# Revit family: RN 11030 Réducteur de pression avec filetage femelle
name_source: partatom
category: Rohrzubehör
units: mm (PartAtom-declared; Revit-internal decimal feet)

## family parameters
Arbeitsebenenbasiert = Nein
Beim Laden mit Abzugskörper schneiden = Nein
Bemaßung runder Anschluss = Durchmesser verwenden
Gemeinsam genutzt = Nein
Immer vertikal = Ja
Teiletyp = Ventil - Zerlegung in

## types (3) — shared parameters
1.010.00.2 Blattnummer der Richtlinie = 17
1.010.00.3 Ausgabedatum (Monat) der Richtlinie = 201601
1.010.00.4 Herstellername = R. Nussbaum AG
1.010.00.5 Revisionsdatum der Datei = 20190528
1.010.00.6 Webadresse des Herstellers = http://www.nussbaum.ch
1.100.00.3 Sortiernummer für Anzeigereihenfolge = 8
1.100.00.4 Produktbezeichnung = Druckminderer
1.960/3L.00.8 Link (URL) = https://www.nussbaum.ch
17.700.00.4 Armaturentyp = 8
17.700.00.7 Maximale Betriebstemperatur TB [°C] = 30
17.700.00.8 Maximaler Betriebsdruck (Arbeitsdruck) ps [1.0 · 105 Pa] = 16
Connector Visibility = Nein
EnclosingSpace Visibility = Nein
Hersteller = R. Nussbauzm AG
URL = https://www.nussbaum.ch

## per-type parameters (varying)
| type | 1.800.00.3 TGA-Nummer | 1.810.00.3 Hersteller-Bestellnummer | 1.810.00.4 DATANORM-Nummer | 1.810.00.5 StLB-Nummer | 1.810.00.6 GTIN-Nummer | 17.700.00.30 Produktbeschreibung | 17.700.00.5 Nennweite DN | 17.700.00.6 kvs-Wert [m3/h] | CONNECTOR0_DIAMETER_dX_0r | CONNECTOR0_dX_00 | CONNECTOR0_dX_01 | CONNECTOR0_ref_dX | CONNECTOR1_DIAMETER_dX_0r | CONNECTOR1_dX_00 | CONNECTOR1_dX_01 | CONNECTOR1_ref_dX | Modell | R. Nussbaum AG 11030.03 de Visibility | R. Nussbaum AG 11030.04 de Visibility | R. Nussbaum AG 11030.05 de Visibility | Typenkommentare |
| DN 10 | 0080050000000000000000000000020070000000000000000100000000 | 11030.03 | 11030.03 | 613.112 | 7612945694799 | 11030.03, Druckreduzierventil mit Innengewinde, Einstellbereich 1 bis 5 bar, DN=1 | 10 | 0.78 | 10 mm  [stored 0.0328084 ft] | 38 mm | 23 mm | 23 mm | 10 mm  [stored 0.0328084 ft] | 23 mm | 38 mm | 23 mm | 11030.03 | Ja | Nein | Nein | Réducteur de pression avec filetage femelleDN 10 |
| DN 15 | 0080050000000000000000000000020070000000000000000200000000 | 11030.04 | 11030.04 | 613.113 | 7612945694805 | 11030.04, Druckreduzierventil mit Innengewinde, Einstellbereich 1 bis 5 bar, DN=1 | 15 | 1.2 | 15 mm | 43 mm | 28 mm | 28 mm | 15 mm | 28 mm | 43 mm | 28 mm | 11030.04 | Nein | Ja | Nein | Réducteur de pression avec filetage femelleDN 15 |
| DN 20 | 0080050000000000000000000000020070000000000000000300000000 | 11030.05 | 11030.05 | 613.114 | 7612945694812 | 11030.05, Druckreduzierventil mit Innengewinde, Einstellbereich 1 bis 5 bar, DN=2 | 20 | 1.62 | 20 mm | 48 mm | 33 mm | 33 mm | 20 mm | 33 mm | 48 mm | 33 mm | 11030.05 | Nein | Nein | Ja | Réducteur de pression avec filetage femelleDN 20 |

note: [stored X ft] marks values corroborated as IEEE doubles in the binary element streams (Revit-internal decimal feet)

## geometry (parser evidence)
native form markers: Sweep x2
no freeform markers — native parametric forms only
